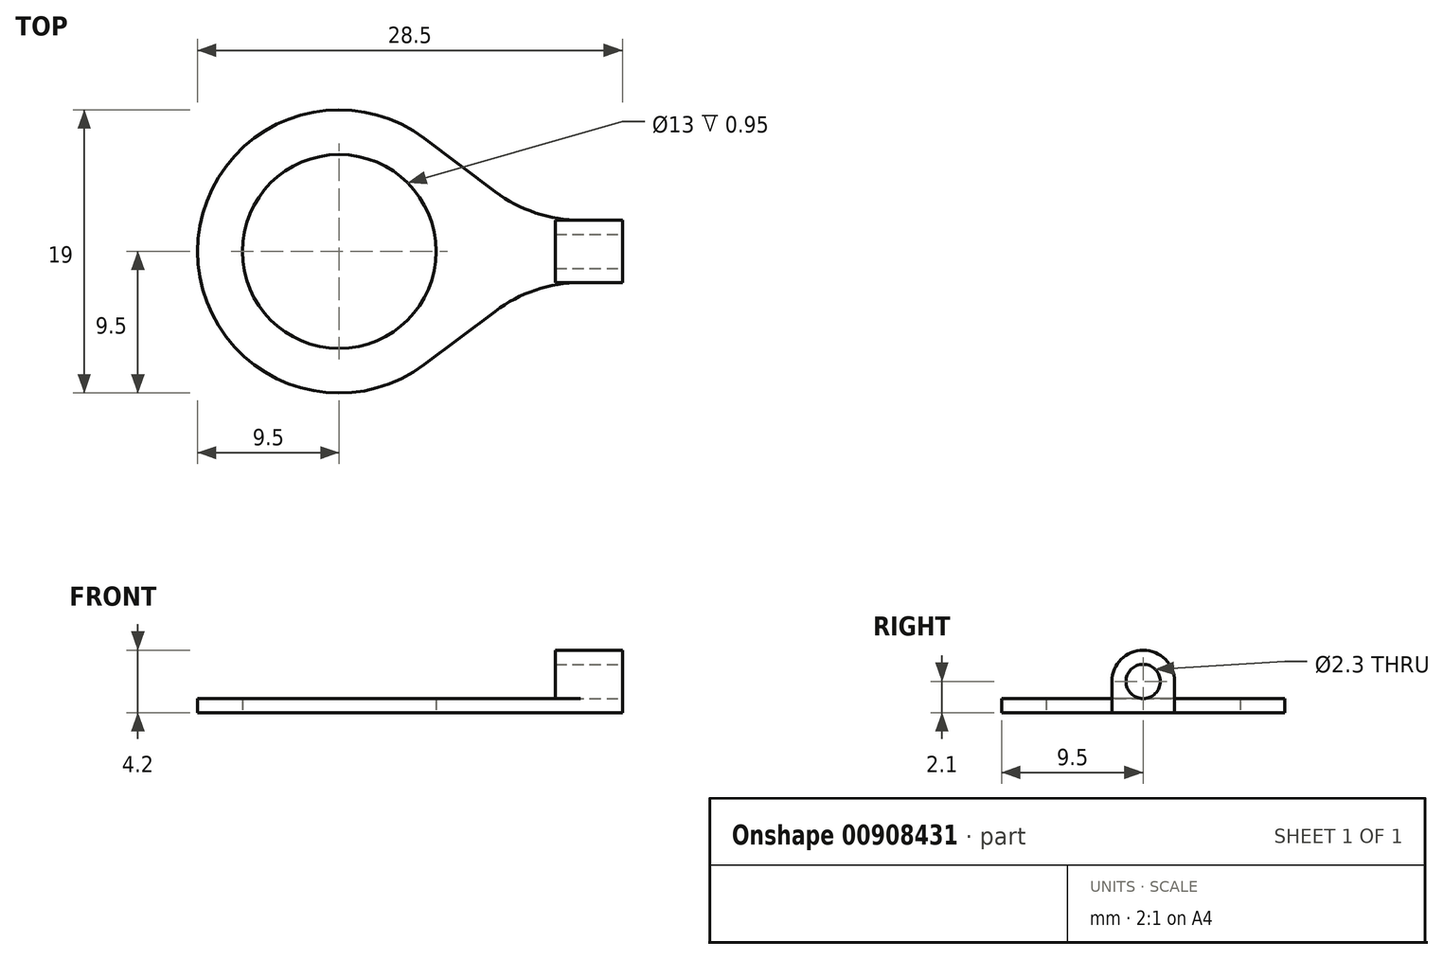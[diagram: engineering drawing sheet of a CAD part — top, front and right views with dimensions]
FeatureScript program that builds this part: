
annotation { "Feature Type Name" : "Feature", "Feature Type Description" : "" }
export const myFeature = defineFeature(function(context is Context, id is Id, definition is map)
    precondition{}
    {
        {
            var Q0;
            Q0=qCreatedBy(makeId("Top.planeOp"),FACE);
            var sketch = newSketch(context, id + "F0", { "sketchPlane" : qUnion([Q0])});
            skLineSegment(sketch, "E0.left", {"start": v(0, 9.5) * mm, "end": v(0, 9.5) * mm});
            skLineSegment(sketch, "E0.right", {"start": v(28.5, 0) * mm, "end": v(28.5, 11.6) * mm});
            skPoint(sketch, "E1.visualSharp", {"position": v(0, 19) * mm});
            skArc(sketch, "E1.filletArc", {"start": v(9.5, 19) * mm, "mid": v(2.78, 16.22) * mm, "end": v(0, 9.5) * mm});
            skPoint(sketch, "E2.visualSharp", {"position": v(0, 0) * mm});
            skArc(sketch, "E2.filletArc", {"start": v(0, 9.5) * mm, "mid": v(2.78, 2.78) * mm, "end": v(9.5, 0) * mm});
            skLineSegment(sketch, "E3.bottom", {"start": v(28.5, 7.4) * mm, "end": v(25.68, 7.4) * mm});
            skLineSegment(sketch, "E3.top", {"start": v(28.5, 11.6) * mm, "end": v(25.68, 11.6) * mm});
            skPoint(sketch, "E3.middle", {"position": v(28.5, 9.5) * mm});
            skArc(sketch, "E4", {"start": v(15.22, 17.09) * mm, "mid": v(0, 9.5) * mm, "end": v(15.22, 1.91) * mm});
            skCircle(sketch, "E5", {"center": v(9.5, 9.5) * mm, "radius": 6.5 * mm});
            skLineSegment(sketch, "E6", {"start": v(19.96, 13.51) * mm, "end": v(15.22, 17.09) * mm});
            skLineSegment(sketch, "E7", {"start": v(19.96, 5.49) * mm, "end": v(15.22, 1.91) * mm});
            skPoint(sketch, "E8.orphan", {"position": v(33, 11.6) * mm});
            skPoint(sketch, "E9.orphan", {"position": v(33, 7.4) * mm});
            skPoint(sketch, "E0.top.end.orphan", {"position": v(28.5, 19) * mm});
            skPoint(sketch, "E10.visualSharp", {"position": v(22.5, 11.6) * mm});
            skArc(sketch, "E10.filletArc", {"start": v(19.96, 13.51) * mm, "mid": v(22.66, 12.1) * mm, "end": v(25.68, 11.6) * mm});
            skPoint(sketch, "E11.visualSharp", {"position": v(22.5, 7.4) * mm});
            skArc(sketch, "E11.filletArc", {"start": v(25.68, 7.4) * mm, "mid": v(22.66, 6.9) * mm, "end": v(19.96, 5.49) * mm});
            skPoint(sketch, "E3.right.end.orphan", {"position": v(24, 11.6) * mm});
            skPoint(sketch, "E3.right.start.orphan", {"position": v(24, 7.4) * mm});
            skSolve(sketch);
        }
        {
            var Q0;
            {var subQ4=sQuery(id+"F0.wireOp",EDGE,"E3.bottom");Q0=makeQuery(id+"F0.imprint","IMPRINT",FACE,{"disambiguationData":[TD([[makeQuery(id+"F0.imprint","IMPRINT",EDGE,{"derivedFrom":subQ4}),-1.0]])]});}
            extrude(context, id + "F1", {"entities" : qUnion([Q0]), "depth" : 0.95 * mm, "offsetDistance" : 25 * mm});
        }
        {
            var Q0;
            Q0=makeQuery(id+"F1.opExtrude","CAP_FACE",FACE,{"disambiguationData":[OSD([sQuery(id+"F0.wireOp",EDGE,"E0.right"),sQuery(id+"F0.wireOp",EDGE,"E3.bottom"),sQuery(id+"F0.wireOp",EDGE,"E3.top"),sQuery(id+"F0.wireOp",EDGE,"E4"),sQuery(id+"F0.wireOp",EDGE,"E5"),sQuery(id+"F0.wireOp",EDGE,"E6"),sQuery(id+"F0.wireOp",EDGE,"E7"),sQuery(id+"F0.wireOp",EDGE,"E10.filletArc"),sQuery(id+"F0.wireOp",EDGE,"E11.filletArc")])],"isStart":false});
            var sketch = newSketch(context, id + "F2", { "sketchPlane" : qUnion([Q0])});
            skLineSegment(sketch, "E12.bottom", {"start": v(28.5, 11.6) * mm, "end": v(24, 11.6) * mm});
            skLineSegment(sketch, "E12.top", {"start": v(28.5, 7.4) * mm, "end": v(24, 7.4) * mm});
            skLineSegment(sketch, "E12.left", {"start": v(28.5, 11.6) * mm, "end": v(28.5, 7.4) * mm});
            skLineSegment(sketch, "E12.right", {"start": v(24, 11.6) * mm, "end": v(24, 7.4) * mm});
            skSolve(sketch);
        }
        {
            var Q0;
            {var subQ0=sQuery(id+"F2.wireOp",EDGE,"E12.left");Q0=makeQuery(id+"F2.imprint","IMPRINT",FACE,{"disambiguationData":[TD([[makeQuery(id+"F2.imprint","IMPRINT",EDGE,{"derivedFrom":subQ0}),1.0]])]});}
            extrude(context, id + "F3", {"entities" : qUnion([Q0]), "operationType" : NewBodyOperationType.ADD, "depth" : 3.25 * mm, "offsetDistance" : 25 * mm});
        }
        {
            var Q0;
            Q0=makeQuery(id+"F3.opExtrude","CAP_EDGE",EDGE,{"disambiguationData":[OSD([sQuery(id+"F2.wireOp",EDGE,"E12.bottom")])],"isStart":false});
            var Q1;
            Q1=makeQuery(id+"F3.opExtrude","CAP_EDGE",EDGE,{"disambiguationData":[OSD([sQuery(id+"F2.wireOp",EDGE,"E12.top")])],"isStart":false});
            fillet(context, id + "F4", {"entities" : qUnion([Q0, Q1]), "radius" : 2.1 * mm, "tangentPropagation" : true, "allowEdgeOverflow" : false});
        }
        {
            var Q0;
            Q0=makeQuery(id+"F3.boolean.opBoolean","MERGE",FACE,{"derivedFrom":[makeQuery(id+"F1.opExtrude","SWEPT_FACE",FACE,{"disambiguationData":[OSD([sQuery(id+"F0.wireOp",EDGE,"E0.right")])]}),makeQuery(id+"F3.opExtrude","SWEPT_FACE",FACE,{"disambiguationData":[OSD([sQuery(id+"F2.wireOp",EDGE,"E12.left")])]})]});
            var sketch = newSketch(context, id + "F5", { "sketchPlane" : qUnion([Q0])});
            skCircle(sketch, "E13", {"center": v(9.5, 2.1) * mm, "radius": 1.15 * mm});
            skSolve(sketch);
        }
        {
            var Q0;
            Q0=makeQuery(id+"F5.imprint","IMPRINT",FACE,{"disambiguationData":[TD([[makeQuery(id+"F5.imprint","IMPRINT",EDGE,{"derivedFrom":sQuery(id+"F5.wireOp",EDGE,"E13")}),1.0]])]});
            extrude(context, id + "F6", {"entities" : qUnion([Q0]), "operationType" : NewBodyOperationType.REMOVE, "oppositeDirection" : true, "depth" : 25 * mm, "offsetDistance" : 25 * mm});
        }
    });
